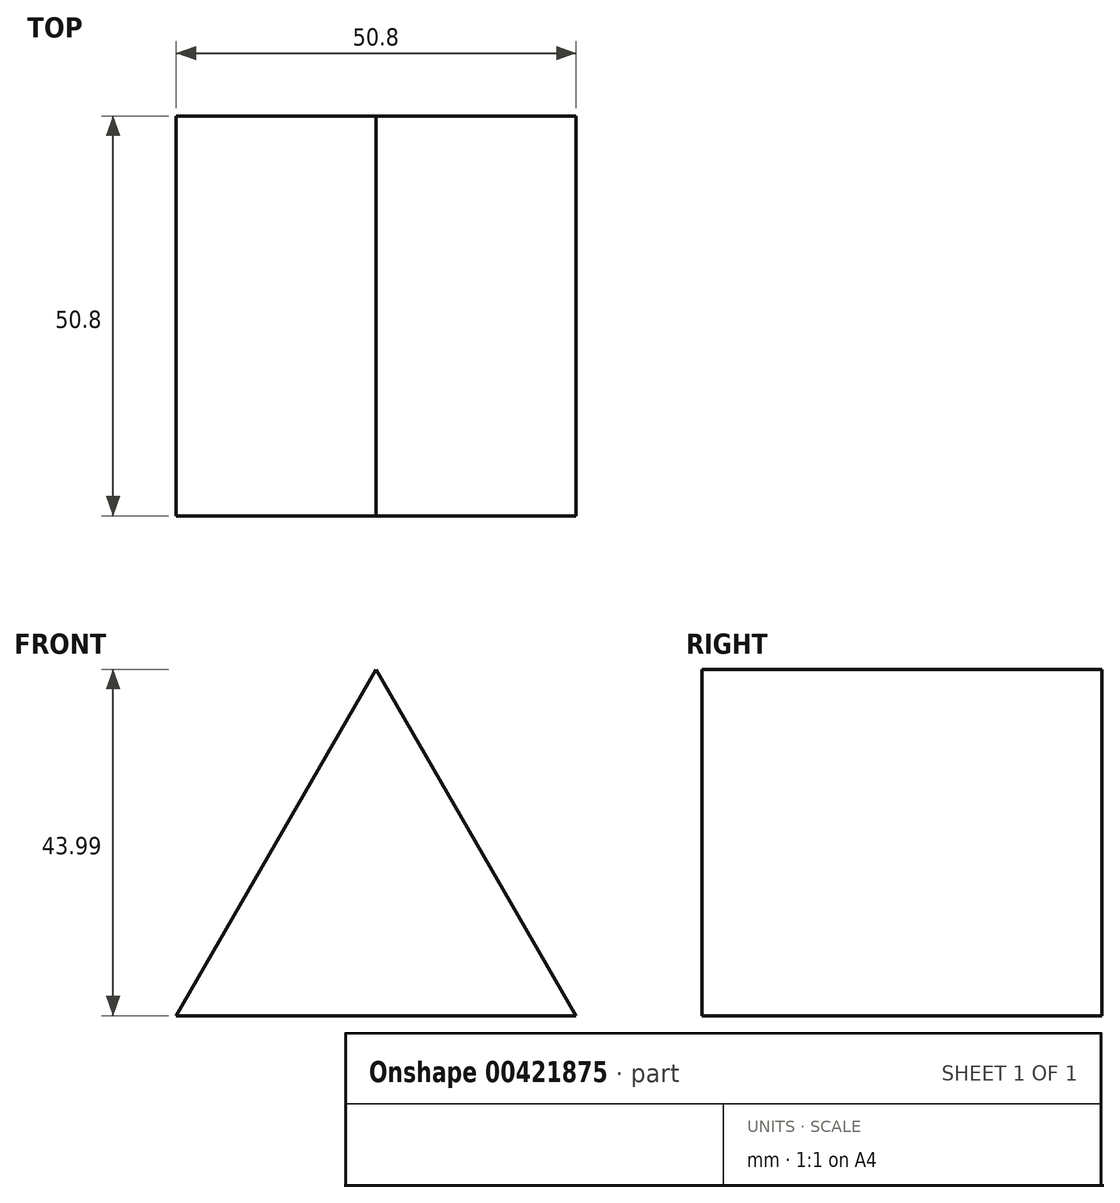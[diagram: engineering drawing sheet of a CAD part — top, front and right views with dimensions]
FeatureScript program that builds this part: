
annotation { "Feature Type Name" : "Feature", "Feature Type Description" : "" }
export const myFeature = defineFeature(function(context is Context, id is Id, definition is map)
    precondition{}
    {
        {
            var Q0;
            Q0=qCreatedBy(makeId("Front.planeOp"),FACE);
            var sketch = newSketch(context, id + "F0", { "sketchPlane" : qUnion([Q0])});
            skLineSegment(sketch, "E0", {"start": v(0, 0) * mm, "end": v(-25.4, 44) * mm});
            skLineSegment(sketch, "E1", {"start": v(-25.4, 44) * mm, "end": v(-50.8, 0) * mm});
            skLineSegment(sketch, "E2", {"start": v(-50.8, 0) * mm, "end": v(0, 0) * mm});
            skSolve(sketch);
        }
        {
            var Q0;
            Q0 = qSketchRegion(id + "F0", true);
            extrude(context, id + "F1", {"entities" : qUnion([Q0]), "depth" : 50.8 * mm});
        }
    });
